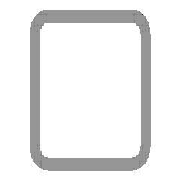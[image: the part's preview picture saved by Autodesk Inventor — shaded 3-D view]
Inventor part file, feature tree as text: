
AUTODESK INVENTOR PART (.ipt)
format: ipt  version: 2022 (Build 260153000, 153)  size: 657,920 bytes
history: native  units: mm (DEFAULTED — no unit token found)
features: other x8, sketch x3, plane x2, surface_op x2, split x1
ambient origin geometry x8: Origin, YZ Plane, XZ Plane, XY Plane, X Axis, Y Axis, Z Axis, Center Point
bodies: Solid1 (feature_tree), Body (feature_tree), Solid5 (feature_tree), Solid6 (feature_tree)
feature tree (16):
  parser-record x1  (decoder bookkeeping rows leaked as tree rows — omitted from the tree; the rows remain in map.json)
  other  "Driven Length"
  other  "Start Plane"
  other  "End Plane"
  plane  "Work Plane4"
  split  "Split1"
  sketch  "Sketch"  dims[d7=4.0mm d9=40.0mm d11=40.0mm d12=2.0mm d13=-0.0mm d14=280.0mm d15=20.0mm d16=20.0mm d17=90.0deg d18=280.0mm d37=5.0mm d38=5.0mm d39=5.0mm d40=5.0mm d41=5.0mm d42=5.0mm d43=5.0mm d44=5.0mm d45=0.0mm d46=5.0mm d47=5.0mm d48=5.0mm d49=5.0mm d50=5.0mm d51=5.0mm d52=5.0mm d53=5.0mm d54=0.0mm]
  sketch  "Sketch3"  dims[d3=280.0mm]
  plane  "Work Plane3"
  sketch  "Sketch4"  dims[d4=0.0mm]
  other  "Srf8"
  other  "Srf9"
  other  "Srf6"
  other  "Srf7"
  surface_op  "Boundary Patch3"
  surface_op  "Boundary Patch4"
